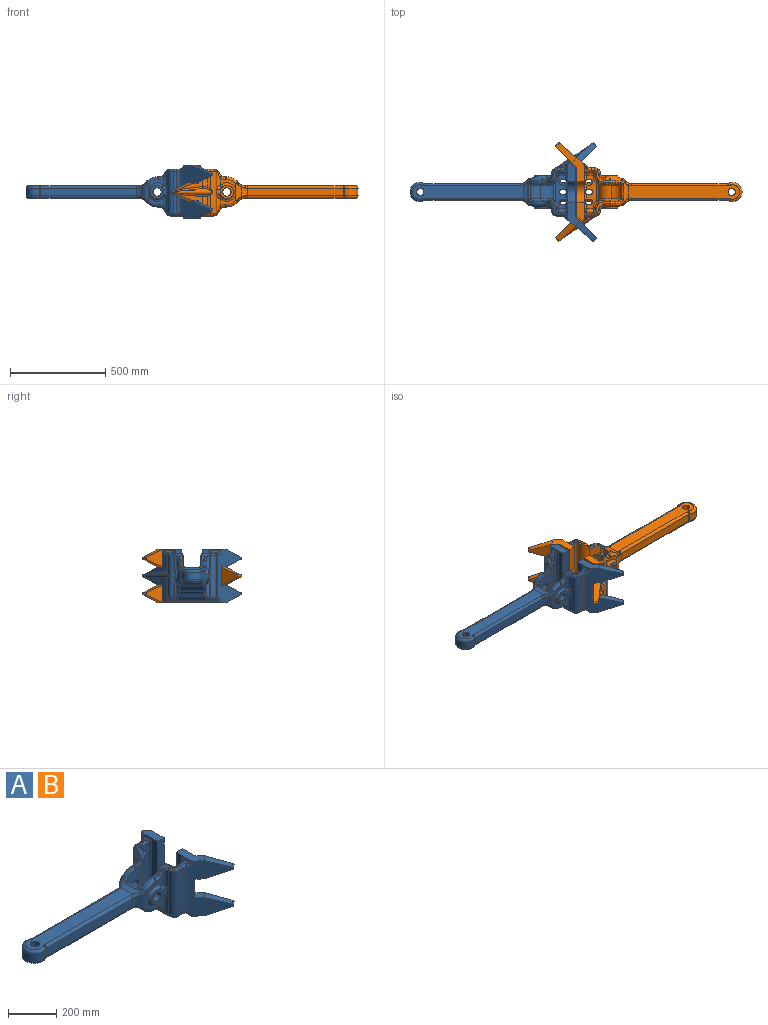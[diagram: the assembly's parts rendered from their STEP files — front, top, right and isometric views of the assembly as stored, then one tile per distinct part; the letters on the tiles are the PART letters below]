
ASSEMBLY  parts=2 mates=1
PART A: 264 faces, bbox 988.1x522.1x283.2 mm
  f0: cylinder r=35mm len=91.5mm, axis (0,0,1), area 2200.2mm2, adj f1,f12,f91,f92,f258
  f1: plane 97.01x18.02mm, normal (0,1,0), area 1677.7mm2, adj f0,f35,f90,f260
  f2: cylinder r=12.7mm len=281.12mm, axis (0,-1,0), area 4841.1mm2, adj f3,f10,f92,f93,f137,f138,f243,f247
  f3: plane 243.38x53.47mm, normal (0,0,-1), area 9442.7mm2, adj f2,f53,f89,f90,f91,f134,f135,f136
  f4: cylinder r=12.7mm len=177.8mm, axis (0,-1,0), area 3084.9mm2, adj f5,f45,f162,f174,f243,f247,f250
  f5: plane 180.47x53.47mm, normal (0,0,1), area 5775.7mm2, adj f4,f152,f158,f159,f161,f170,f171,f173
  f6: cylinder r=79.26mm len=62.88mm, axis (0,-1,0), area 746.2mm2, adj f25,f47,f107,f108,f230,f231
  f7: plane 114.5x114.5mm, normal (0.71,0.71,0), area 9766.8mm2, adj f10,f23,f209,f210,f211,f212
  f8: plane 280.16x148.86mm, normal (-0.64,-0.77,0), area 27221.7mm2, adj f9,f10,f98,f119,f120,f138,f207,f208
  f9: plane 125.59x65.04mm, normal (0,0,1), area 4853mm2, adj f8,f11,f23,f45,f120,f177,f208
  f10: plane 334.61x65.11mm, normal (0,0,-1), area 12374.9mm2, adj f2,f7,f8,f12,f23,f93,f138,f206
  f11: plane 114.5x114.5mm, normal (0.71,0.71,0), area 9766.8mm2, adj f9,f23,f207,f208,f214,f215
  f12: plane 280.16x148.86mm, normal (-0.64,0.77,0), area 10301.5mm2, adj f0,f10,f40,f41,f73,f74,f93,f200
  f13: plane 114.5x114.5mm, normal (0.71,-0.71,0), area 9766.8mm2, adj f23,f201,f202,f203,f204,f205
  f14: plane 81.6x66.55mm, normal (0,-1,0), area 1880.2mm2, adj f19,f96,f127,f128,f129,f188
  f15: plane 81.6x66.55mm, normal (0,1,0), area 1880.2mm2, adj f17,f38,f62,f63,f64,f195
  f16: plane 96.87x2.23mm, normal (-1,0,0), area 209.3mm2, adj f35,f37,f87,f192
  f17: cylinder r=20mm len=86.51mm, axis (0,0,1), area 2196.7mm2, adj f15,f36,f65,f66,f197
  f18: plane 91.49x2.24mm, normal (-1,0,0), area 197.4mm2, adj f21,f94,f113,f183
  f19: cylinder r=20mm len=91.89mm, axis (0,0,1), area 2292.1mm2, adj f14,f95,f130,f131,f189
  f20: plane 81.6x66.55mm, normal (0,1,0), area 1880.2mm2, adj f37,f38,f82,f83,f84,f191
  f21: cylinder r=20mm len=86.51mm, axis (0,0,1), area 2196.7mm2, adj f18,f22,f111,f112,f182
  f22: plane 81.6x66.55mm, normal (0,-1,0), area 1880.2mm2, adj f21,f96,f108,f109,f110,f184
  f23: plane 279.4x254mm, normal (1,0,0), area 51653.5mm2, adj f7,f9,f10,f11,f13,f40,f175,f176
  f24: plane 9.53x5.51mm, normal (0,0,1), area 52.5mm2, adj f26,f28,f63,f224
  f25: plane 9.53x5.51mm, normal (0,0,1), area 52.5mm2, adj f6,f27,f109,f232
  f26: cylinder r=38.1mm len=33.89mm, axis (0,-1,0), area 441.2mm2, adj f24,f29,f64,f65,f222,f223
  f27: cylinder r=38.1mm len=33.89mm, axis (0,-1,0), area 441.2mm2, adj f25,f30,f110,f111,f233,f234
  f28: cylinder r=79.26mm len=62.88mm, axis (0,-1,0), area 746.2mm2, adj f24,f47,f61,f62,f225,f226
  f29: cylinder r=38.1mm len=58.66mm, axis (0,-1,0), area 932.8mm2, adj f26,f31,f66,f67,f68,f219,f220,f221
  f30: cylinder r=38.1mm len=58.66mm, axis (0,-1,0), area 932.8mm2, adj f27,f44,f112,f113,f114,f235,f236,f237
  f31: plane 53.7x28.24mm, normal (0,0,1), area 441.9mm2, adj f29,f32,f69,f70,f71,f217,f218
  f32: cylinder r=12.7mm len=51.66mm, axis (0,-1,0), area 636.2mm2, adj f31,f45,f72,f73,f216
  f33: cylinder r=12.7mm len=51.66mm, axis (0,-1,0), area 636.2mm2, adj f44,f45,f118,f119,f240
  f34: cylinder r=50.8mm len=101.6mm, axis (0,0,1), area 8478.6mm2, adj f54,f55,f75,f101
  f35: cylinder r=31.75mm len=222.25mm, axis (0,0,1), area 10734.8mm2, adj f1,f16,f36,f42,f68,f69,f88,f89
  f36: plane 91.49x2.24mm, normal (-1,0,0), area 197.4mm2, adj f17,f35,f67,f196
  f37: cylinder r=20mm len=91.89mm, axis (0,0,1), area 2292.1mm2, adj f16,f20,f85,f86,f190
  f38: cylinder r=38.1mm len=93mm, axis (0,0,1), area 2472.3mm2, adj f15,f20,f43,f60,f61,f80,f81,f193
  f39: plane 503.39x41.28mm, normal (0,1,0), area 20777.3mm2, adj f43,f54,f57,f77
  f40: plane 101x38.1mm, normal (0,0,1), area 3409mm2, adj f12,f23,f45,f74,f176,f200
  f41: cylinder r=35mm len=83.63mm, axis (0,0,1), area 1986.2mm2, adj f12,f42,f71,f72,f257
  f42: plane 90.66x18.02mm, normal (0,1,0), area 1556.8mm2, adj f35,f41,f70,f259,f261
  f43: cylinder r=38.1mm len=55.19mm, axis (0,0,1), area 1571.9mm2, adj f38,f39,f58,f59,f78,f79
  f44: plane 53.7x28.24mm, normal (0,0,1), area 441.9mm2, adj f30,f33,f115,f116,f117,f238,f239
  f45: plane 281.12x228.6mm, normal (-1,0,0), area 21987.1mm2, adj f4,f9,f32,f33,f40,f74,f120,f145
  f46: plane 583.16x76.2mm, normal (0,0,1), area 35909.7mm2, adj f47,f55,f56,f57,f58,f102,f103,f104
  f47: cylinder r=38.1mm len=119.58mm, axis (0,-1,0), area 2785.4mm2, adj f6,f28,f46,f59,f60,f105,f106,f227
  f48: cylinder r=38.1mm len=132.35mm, axis (0,-1,0), area 5593.3mm2, adj f49,f53,f84,f85,f129,f130
  f49: plane 120.65x5.51mm, normal (0,0,-1), area 665.3mm2, adj f48,f50,f83,f128
  f50: cylinder r=79.26mm len=120.65mm, axis (0,-1,0), area 8758mm2, adj f49,f51,f81,f82,f126,f127
  f51: cylinder r=38.1mm len=119.58mm, axis (0,-1,0), area 3335.1mm2, adj f50,f52,f79,f80,f124,f125
  f52: plane 583.16x76.2mm, normal (0,0,-1), area 35909.7mm2, adj f51,f75,f76,f77,f78,f121,f122,f123
  f53: cylinder r=38.1mm len=223.5mm, axis (0,-1,0), area 7594.5mm2, adj f3,f48,f86,f87,f88,f131,f132,f133
  f54: cylinder r=12.7mm len=41.28mm, axis (0,0,1), area 236.4mm2, adj f34,f39,f56,f76
  f55: torus R=38.1mm, axis (0,0,-1), area 3725.6mm2, adj f34,f46,f56,f102
  f56: torus R=25.4mm, axis (0,0,-1), area 155.8mm2, adj f46,f54,f55,f57
  f57: cylinder r=12.7mm len=503.39mm, axis (1,0,0), area 10042.1mm2, adj f39,f46,f56,f58
  f58: torus R=50.8mm, axis (0,0,-1), area 237.8mm2, adj f43,f46,f57,f59
  f59: bspline ~29.37x28.28mm, area 428.2mm2, adj f43,f47,f58,f60
  f60: bspline ~26.43x23.64mm, area 375.8mm2, adj f38,f47,f59,f61
  f61: bspline ~23.24x21.94mm, area 188.3mm2, adj f28,f38,f60,f62
  f62: torus R=66.56mm, axis (0,-1,0), area 1187.4mm2, adj f15,f28,f61,f63
  f63: cylinder r=12.7mm len=12.7mm, axis (1,0,0), area 110mm2, adj f15,f24,f62,f64
  f64: torus R=50.8mm, axis (0,-1,0), area 506.7mm2, adj f15,f26,f63,f65
  f65: bspline ~30.18x20.89mm, area 329.8mm2, adj f17,f26,f64,f66
  f66: bspline ~32.15x27.43mm, area 525.3mm2, adj f17,f29,f65,f67
  f67: cylinder r=12.7mm len=12.26mm, axis (0,-1,0), area 36.9mm2, adj f29,f36,f66,f68
  f68: bspline ~29.83x21.49mm, area 432.7mm2, adj f29,f35,f67,f69
  f69: torus R=19.05mm, axis (0,0,-1), area 384.7mm2, adj f31,f35,f68,f70
  f70: cylinder r=12.7mm len=18.02mm, axis (1,0,0), area 359.4mm2, adj f31,f42,f69,f71
  f71: torus R=47.7mm, axis (0,0,-1), area 402.5mm2, adj f31,f41,f70,f72
  f72: bspline ~17.57x13.82mm, area 107.2mm2, adj f32,f41,f71,f73
  f73: bspline ~29.24x26.42mm, area 389.8mm2, adj f12,f32,f72,f74
  f74: cylinder r=12.7mm len=9.73mm, axis (0,0,1), area 70.4mm2, adj f12,f40,f45,f73
  f75: torus R=38.1mm, axis (0,0,-1), area 3725.6mm2, adj f34,f52,f76,f121
  f76: torus R=25.4mm, axis (0,0,-1), area 155.8mm2, adj f52,f54,f75,f77
  f77: cylinder r=12.7mm len=503.39mm, axis (-1,0,0), area 10042.1mm2, adj f39,f52,f76,f78
  f78: torus R=50.8mm, axis (0,0,-1), area 237.8mm2, adj f43,f52,f77,f79
  f79: bspline ~29.37x28.28mm, area 428.2mm2, adj f43,f51,f78,f80
  f80: bspline ~29.16x24.11mm, area 375.8mm2, adj f38,f51,f79,f81
  f81: bspline ~23.24x21.94mm, area 188.3mm2, adj f38,f50,f80,f82
  f82: torus R=66.56mm, axis (0,-1,0), area 1187.4mm2, adj f20,f50,f81,f83
  f83: cylinder r=12.7mm len=12.7mm, axis (-1,0,0), area 110mm2, adj f20,f49,f82,f84
  f84: torus R=50.8mm, axis (0,-1,0), area 506.7mm2, adj f20,f48,f83,f85
  f85: bspline ~33.53x21.8mm, area 382.9mm2, adj f37,f48,f84,f86
  f86: bspline ~30.68x28.07mm, area 468.1mm2, adj f37,f53,f85,f87
  f87: cylinder r=12.7mm len=11.77mm, axis (0,-1,0), area 33.5mm2, adj f16,f53,f86,f88
  f88: bspline ~30.06x24.62mm, area 512.1mm2, adj f35,f53,f87,f89
  f89: torus R=19.05mm, axis (0,0,1), area 283.4mm2, adj f3,f35,f88,f90
  f90: cylinder r=12.7mm len=18.02mm, axis (-1,0,0), area 359.4mm2, adj f1,f3,f89,f91
  f91: torus R=47.7mm, axis (0,0,1), area 402.5mm2, adj f0,f3,f90,f92
  f92: bspline ~19.3x15.05mm, area 107.2mm2, adj f0,f2,f91,f93
  f93: bspline ~26.42x25.93mm, area 389.8mm2, adj f2,f10,f12,f92
  f94: cylinder r=31.75mm len=222.25mm, axis (0,0,1), area 11012.1mm2, adj f18,f95,f99,f114,f115,f133,f134,f185
  f95: plane 96.87x2.23mm, normal (-1,0,0), area 209.3mm2, adj f19,f94,f132,f187
  f96: cylinder r=38.1mm len=93mm, axis (0,0,1), area 2472.3mm2, adj f14,f22,f100,f106,f107,f125,f126,f186
  f97: plane 503.39x41.28mm, normal (0,-1,0), area 20777.3mm2, adj f100,f101,f103,f122
  f98: cylinder r=35mm len=224.45mm, axis (0,0,1), area 5437.9mm2, adj f8,f99,f117,f118,f136,f137
  f99: plane 222.25x18.02mm, normal (0,-1,0), area 4004mm2, adj f94,f98,f116,f135
  f100: cylinder r=38.1mm len=55.19mm, axis (0,0,1), area 1571.9mm2, adj f96,f97,f104,f105,f123,f124
  f101: cylinder r=12.7mm len=41.28mm, axis (0,0,1), area 236.4mm2, adj f34,f97,f102,f121
  f102: torus R=25.4mm, axis (0,0,-1), area 155.8mm2, adj f46,f55,f101,f103
  f103: cylinder r=12.7mm len=503.39mm, axis (1,0,0), area 10042.1mm2, adj f46,f97,f102,f104
  f104: torus R=50.8mm, axis (0,0,-1), area 237.8mm2, adj f46,f100,f103,f105
  f105: bspline ~29.37x28.28mm, area 428.2mm2, adj f47,f100,f104,f106
  f106: bspline ~29.16x24.11mm, area 375.8mm2, adj f47,f96,f105,f107
  f107: bspline ~21.91x21.39mm, area 188.3mm2, adj f6,f96,f106,f108
  f108: torus R=66.56mm, axis (0,1,0), area 1187.4mm2, adj f6,f22,f107,f109
  f109: cylinder r=12.7mm len=12.7mm, axis (1,0,0), area 110mm2, adj f22,f25,f108,f110
  f110: torus R=50.8mm, axis (0,1,0), area 506.7mm2, adj f22,f27,f109,f111
  f111: bspline ~30.18x20.89mm, area 329.8mm2, adj f21,f27,f110,f112
  f112: bspline ~32.15x27.43mm, area 525.3mm2, adj f21,f30,f111,f113
  f113: cylinder r=12.7mm len=12.26mm, axis (0,1,0), area 36.9mm2, adj f18,f30,f112,f114
  f114: bspline ~29.83x21.49mm, area 432.7mm2, adj f30,f94,f113,f115
  f115: torus R=19.05mm, axis (0,0,-1), area 384.7mm2, adj f44,f94,f114,f116
  f116: cylinder r=12.7mm len=18.02mm, axis (1,0,0), area 359.4mm2, adj f44,f99,f115,f117
  f117: torus R=47.7mm, axis (0,0,-1), area 402.5mm2, adj f44,f98,f116,f118
  f118: bspline ~18.17x13.82mm, area 107.2mm2, adj f33,f98,f117,f119
  f119: bspline ~29.24x26.42mm, area 389.8mm2, adj f8,f33,f118,f120
  f120: cylinder r=12.7mm len=9.73mm, axis (0,0,1), area 70.4mm2, adj f8,f9,f45,f119
  f121: torus R=25.4mm, axis (0,0,-1), area 155.8mm2, adj f52,f75,f101,f122
  f122: cylinder r=12.7mm len=503.39mm, axis (-1,0,0), area 10042.1mm2, adj f52,f97,f121,f123
  f123: torus R=50.8mm, axis (0,0,-1), area 237.8mm2, adj f52,f100,f122,f124
  f124: bspline ~29.37x28.28mm, area 428.2mm2, adj f51,f100,f123,f125
  f125: bspline ~26.43x23.64mm, area 375.8mm2, adj f51,f96,f124,f126
  f126: bspline ~25.44x24.69mm, area 188.3mm2, adj f50,f96,f125,f127
  f127: torus R=66.56mm, axis (0,1,0), area 1187.4mm2, adj f14,f50,f126,f128
  f128: cylinder r=12.7mm len=12.7mm, axis (-1,0,0), area 110mm2, adj f14,f49,f127,f129
  f129: torus R=50.8mm, axis (0,1,0), area 506.7mm2, adj f14,f48,f128,f130
  f130: bspline ~33.53x21.8mm, area 382.9mm2, adj f19,f48,f129,f131
  f131: bspline ~30.68x28.07mm, area 468.1mm2, adj f19,f53,f130,f132
  f132: cylinder r=12.7mm len=11.77mm, axis (0,1,0), area 33.5mm2, adj f53,f95,f131,f133
  f133: bspline ~32.65x24.62mm, area 512.1mm2, adj f53,f94,f132,f134
  f134: torus R=19.05mm, axis (0,0,1), area 283.4mm2, adj f3,f94,f133,f135
  f135: cylinder r=12.7mm len=18.02mm, axis (-1,0,0), area 359.4mm2, adj f3,f99,f134,f136
  f136: torus R=47.7mm, axis (0,0,1), area 402.5mm2, adj f3,f98,f135,f137
  f137: bspline ~18.17x13.82mm, area 107.2mm2, adj f2,f98,f136,f138
  f138: bspline ~26.42x25.93mm, area 389.8mm2, adj f2,f8,f10,f137
  f139: cylinder r=12.7mm len=203.2mm, axis (0,0,-1), area 4053.7mm2, adj f140,f143,f160,f218,f219
  f140: plane 203.2x6.35mm, normal (1,0,0), area 1290.3mm2, adj f139,f148,f159,f220
  f141: cylinder r=12.7mm len=203.2mm, axis (0,0,-1), area 4053.7mm2, adj f142,f144,f172,f237,f238
  f142: plane 203.2x6.35mm, normal (1,0,0), area 1290.3mm2, adj f141,f164,f171,f236
  f143: plane 203.2x34.93mm, normal (0,-1,0), area 7096.8mm2, adj f139,f145,f161,f217
  f144: plane 203.2x34.93mm, normal (0,1,0), area 7096.8mm2, adj f141,f146,f173,f239
  f145: cylinder r=12.7mm len=222.25mm, axis (0,0,-1), area 4191.8mm2, adj f45,f143,f162,f216
  f146: cylinder r=12.7mm len=222.25mm, axis (0,0,-1), area 4191.8mm2, adj f45,f144,f174,f240
  f147: plane 138.21x85.73mm, normal (0,-1,0), area 7728.2mm2, adj f148,f153,f154,f155,f198,f223,f224,f225
  f148: cylinder r=38.1mm len=203.2mm, axis (0,0,-1), area 11163.9mm2, adj f140,f147,f156,f158,f221,f222
  f149: plane 63.5x38.29mm, normal (1,0,0), area 2431.3mm2, adj f150,f153,f165,f228
  f150: cylinder r=50.8mm len=63.5mm, axis (0,-1,0), area 5364.9mm2, adj f149,f151,f154,f166
  f151: cylinder r=63.5mm len=91.32mm, axis (0,-1,0), area 6007.4mm2, adj f150,f152,f155,f156,f167,f168
  f152: cylinder r=12.7mm len=91.32mm, axis (0,-1,0), area 1435.5mm2, adj f5,f151,f157,f169
  f153: cylinder r=12.7mm len=57.79mm, axis (0,0,-1), area 921.2mm2, adj f147,f149,f154,f226,f227
  f154: torus R=38.1mm, axis (0,-1,0), area 1532.3mm2, adj f147,f150,f153,f155
  f155: torus R=76.2mm, axis (0,-1,0), area 816.2mm2, adj f147,f151,f154,f156
  f156: bspline ~53.16x37.53mm, area 751.6mm2, adj f148,f151,f155,f157
  f157: sphere r=12.7mm, area 120mm2, adj f152,f156,f158
  f158: torus R=50.8mm, axis (0,0,-1), area 692.6mm2, adj f5,f148,f157,f159
  f159: cylinder r=12.7mm len=12.7mm, axis (0,-1,0), area 126.7mm2, adj f5,f140,f158,f160
  f160: sphere r=12.7mm, area 253.4mm2, adj f139,f159,f161
  f161: cylinder r=12.7mm len=34.93mm, axis (-1,0,0), area 696.7mm2, adj f5,f143,f160,f162
  f162: sphere r=12.7mm, area 253.4mm2, adj f4,f145,f161
  f163: plane 138.21x85.73mm, normal (0,1,0), area 7728.2mm2, adj f164,f165,f166,f167,f199,f231,f232,f233
  f164: cylinder r=38.1mm len=203.2mm, axis (0,0,-1), area 11163.9mm2, adj f142,f163,f168,f170,f234,f235
  f165: cylinder r=12.7mm len=57.79mm, axis (0,0,-1), area 921.2mm2, adj f149,f163,f166,f229,f230
  f166: torus R=38.1mm, axis (0,1,0), area 1532.3mm2, adj f150,f163,f165,f167
  f167: torus R=76.2mm, axis (0,1,0), area 816.2mm2, adj f151,f163,f166,f168
  f168: bspline ~53.16x37.53mm, area 751.6mm2, adj f151,f164,f167,f169
  f169: sphere r=12.7mm, area 120mm2, adj f152,f168,f170
  f170: torus R=50.8mm, axis (0,0,-1), area 692.6mm2, adj f5,f164,f169,f171
  f171: cylinder r=12.7mm len=12.7mm, axis (0,1,0), area 126.7mm2, adj f5,f142,f170,f172
  f172: sphere r=12.7mm, area 253.4mm2, adj f141,f171,f173
  f173: cylinder r=12.7mm len=34.93mm, axis (-1,0,0), area 696.7mm2, adj f5,f144,f172,f174
  f174: sphere r=12.7mm, area 253.4mm2, adj f4,f146,f173
  f175: cylinder r=53.98mm len=107.95mm, axis (1,0,0), area 6460.5mm2, adj f23,f45,f176,f177
  f176: plane 136.53x38.1mm, normal (0,-1,0), area 5201.6mm2, adj f23,f40,f45,f175
  f177: plane 136.53x38.1mm, normal (0,1,0), area 5201.6mm2, adj f9,f23,f45,f175
  f178: plane 72.36x72.36mm, normal (0,-1,0), area 2456.3mm2, adj f179,f182,f183,f184,f185,f187,f188,f189
  f179: cylinder r=35.72mm len=12.88mm, axis (0,-1,0), area 0mm2, adj f178,f186
  f180: cylinder r=35.72mm len=12.88mm, axis (0,1,0), area 0mm2, adj f181,f193
  f181: plane 72.36x72.36mm, normal (0,1,0), area 2456.3mm2, adj f180,f190,f191,f192,f194,f195,f196,f197
  f182: bspline ~28.91x20.71mm, area 556.1mm2, adj f21,f178,f183,f184
  f183: bspline ~30.1x22.44mm, area 89.1mm2, adj f18,f178,f182,f185
  f184: torus R=48.42mm, axis (0,1,0), area 1743.8mm2, adj f22,f178,f182,f186
  f185: bspline ~34.19x27.95mm, area 679.7mm2, adj f94,f178,f183,f187
  f186: bspline ~27.73x13.98mm, area 289.5mm2, adj f96,f179,f184,f188
  f187: bspline ~30.65x22.38mm, area 89.1mm2, adj f95,f178,f185,f189
  f188: torus R=48.42mm, axis (0,1,0), area 1743.8mm2, adj f14,f178,f186,f189
  f189: bspline ~28.91x20.71mm, area 556.2mm2, adj f19,f178,f187,f188
  f190: bspline ~28.91x20.71mm, area 556.2mm2, adj f37,f181,f191,f192
  f191: torus R=48.42mm, axis (0,-1,0), area 1743.8mm2, adj f20,f181,f190,f193
  f192: bspline ~30.65x22.38mm, area 89.1mm2, adj f16,f181,f190,f194
  f193: bspline ~27.73x13.98mm, area 289.5mm2, adj f38,f180,f191,f195
  f194: bspline ~34.19x27.95mm, area 679.7mm2, adj f35,f181,f192,f196
  f195: torus R=48.42mm, axis (0,-1,0), area 1743.8mm2, adj f15,f181,f193,f197
  f196: bspline ~29.9x22.37mm, area 89.1mm2, adj f36,f181,f194,f197
  f197: bspline ~28.91x20.71mm, area 556.1mm2, adj f17,f181,f195,f196
  f198: cylinder r=22.23mm len=44.45mm, axis (0,-1,0), area 5763.8mm2, adj f147,f181
  f199: cylinder r=22.23mm len=44.45mm, axis (0,-1,0), area 5763.8mm2, adj f163,f178
  f200: plane 93.66x27.98mm, normal (0.71,0.71,0), area 3705.9mm2, adj f12,f23,f40,f201
  f201: plane 54.92x52.56mm, normal (0,0,1), area 1444mm2, adj f12,f13,f200,f202
  f202: plane 110.11x102.72mm, normal (0.22,0.22,0.95), area 3907.2mm2, adj f12,f13,f201,f203
  f203: cylinder r=6.35mm len=21.29mm, axis (0.71,-0.71,0), area 408.5mm2, adj f12,f13,f202,f204
  f204: plane 110.11x102.72mm, normal (0.22,0.22,-0.95), area 3907.2mm2, adj f12,f13,f203,f205
  f205: plane 54.92x52.56mm, normal (0,0,-1), area 1444mm2, adj f12,f13,f204,f206
  f206: plane 93.66x27.98mm, normal (0.71,0.71,0), area 3705.9mm2, adj f10,f12,f23,f205
  f207: cylinder r=6.35mm len=21.29mm, axis (0.71,0.71,0), area 408.5mm2, adj f8,f11,f208,f215
  f208: plane 110.11x102.72mm, normal (0.22,-0.22,0.95), area 3907.2mm2, adj f8,f9,f11,f207
  f209: plane 110.11x102.72mm, normal (0.22,-0.22,-0.95), area 3907.2mm2, adj f7,f8,f10,f210
  f210: cylinder r=6.35mm len=21.29mm, axis (0.71,0.71,0), area 408.5mm2, adj f7,f8,f209,f211
  f211: plane 110.11x102.72mm, normal (0.22,-0.22,0.95), area 3907.2mm2, adj f7,f8,f210,f212
  f212: plane 54.92x52.56mm, normal (0,0,1), area 1444mm2, adj f7,f8,f211,f213
  f213: plane 95.25x27.98mm, normal (0.71,-0.71,0), area 3768.7mm2, adj f8,f23,f212,f214
  f214: plane 54.92x52.56mm, normal (0,0,-1), area 1444mm2, adj f8,f11,f213,f215
  f215: plane 110.11x102.72mm, normal (0.22,-0.22,-0.95), area 3907.2mm2, adj f8,f11,f207,f214
  f216: bspline ~19.05x19.05mm, area 145.9mm2, adj f32,f145,f217
  f217: cylinder r=6.35mm len=34.93mm, axis (1,0,0), area 348.4mm2, adj f31,f143,f216,f218
  f218: torus R=19.05mm, axis (0,0,-1), area 209.7mm2, adj f31,f139,f217,f219
  f219: bspline ~7.42x6.91mm, area 25.5mm2, adj f29,f139,f218,f220
  f220: cylinder r=6.35mm len=6.4mm, axis (0,-1,0), area 63.7mm2, adj f29,f140,f219,f221
  f221: bspline ~42.87x41.71mm, area 678.4mm2, adj f29,f148,f220,f222
  f222: bspline ~16.68x14.53mm, area 69.9mm2, adj f26,f148,f221,f223
  f223: torus R=44.45mm, axis (0,-1,0), area 376.8mm2, adj f26,f147,f222,f224
  f224: cylinder r=6.35mm len=6.35mm, axis (1,0,0), area 55mm2, adj f24,f147,f223,f225
  f225: torus R=72.91mm, axis (0,-1,0), area 503.2mm2, adj f28,f147,f224,f226
  f226: bspline ~21.98x21.35mm, area 217.8mm2, adj f28,f153,f225,f227
  f227: bspline ~16.72x15.7mm, area 166.7mm2, adj f47,f153,f226,f228
  f228: cylinder r=6.35mm len=63.5mm, axis (0,-1,0), area 927.4mm2, adj f47,f149,f227,f229
  f229: bspline ~16.72x15.7mm, area 166.7mm2, adj f47,f165,f228,f230
  f230: bspline ~21.13x20.67mm, area 217.8mm2, adj f6,f165,f229,f231
  f231: torus R=72.91mm, axis (0,1,0), area 503.2mm2, adj f6,f163,f230,f232
  f232: cylinder r=6.35mm len=6.35mm, axis (-1,0,0), area 55mm2, adj f25,f163,f231,f233
  f233: torus R=44.45mm, axis (0,1,0), area 376.8mm2, adj f27,f163,f232,f234
  f234: bspline ~16.68x14.53mm, area 69.9mm2, adj f27,f164,f233,f235
  f235: bspline ~42.75x40.46mm, area 678.4mm2, adj f30,f164,f234,f236
  f236: cylinder r=6.35mm len=6.4mm, axis (0,-1,0), area 63.7mm2, adj f30,f142,f235,f237
  f237: bspline ~7.42x6.91mm, area 25.5mm2, adj f30,f141,f236,f238
  f238: torus R=19.05mm, axis (0,0,-1), area 209.7mm2, adj f44,f141,f237,f239
  f239: cylinder r=6.35mm len=34.93mm, axis (-1,0,0), area 348.4mm2, adj f44,f144,f238,f240
  f240: bspline ~19.05x19.05mm, area 145.9mm2, adj f33,f146,f239
  f241: plane 25.4x12.7mm, normal (0,1,0), area 322.6mm2, adj f3,f5,f243,f244
  f242: plane 25.4x12.7mm, normal (0,-1,0), area 322.6mm2, adj f3,f5,f243,f244
  f243: cylinder r=12.7mm len=30.97mm, axis (0,0,1), area 1097.2mm2, adj f2,f3,f4,f5,f241,f242
  f244: cylinder r=12.7mm len=25.4mm, axis (0,0,1), area 1013.4mm2, adj f3,f5,f241,f242
  f245: plane 25.4x12.7mm, normal (0,0.89,0.45), area 360.7mm2, adj f3,f5,f247,f248
  f246: plane 25.4x12.7mm, normal (0,-0.89,-0.45), area 360.7mm2, adj f3,f5,f247,f248
  f247: cylinder r=12.7mm len=48.12mm, axis (0,-0.45,0.89), area 1226.8mm2, adj f2,f3,f4,f5,f245,f246
  f248: cylinder r=12.7mm len=48.12mm, axis (0,-0.45,0.89), area 1133mm2, adj f3,f5,f245,f246
  f249: cylinder r=12.7mm len=48.12mm, axis (0,0.45,0.89), area 1133mm2, adj f3,f5,f251,f252
  f250: cylinder r=12.7mm len=48.12mm, axis (0,0.45,0.89), area 1226.8mm2, adj f2,f3,f4,f5,f251,f252
  f251: plane 25.4x12.7mm, normal (0,-0.89,0.45), area 360.7mm2, adj f3,f5,f249,f250
  f252: plane 25.4x12.7mm, normal (0,0.89,-0.45), area 360.7mm2, adj f3,f5,f249,f250
  f253: cylinder r=12.7mm len=199.93mm, axis (-0.83,-0.56,0), area 4870.6mm2, adj f254,f256,f258,f260,f261,f262
  f254: plane 100.53x67.17mm, normal (-0.34,0.51,0.79), area 857.6mm2, adj f253,f255,f257,f259
  f255: cylinder r=12.7mm len=77.7mm, axis (-0.76,-0.64,0.08), area 1131.1mm2, adj f12,f254,f256,f257
  f256: bspline ~163.1x130.84mm, area 2841.9mm2, adj f12,f253,f255,f258
  f257: bspline ~22.5x12.96mm, area 250mm2, adj f41,f254,f255,f259
  f258: bspline ~26.05x17.36mm, area 350.1mm2, adj f0,f253,f256,f260
  f259: cylinder r=12.7mm len=16.66mm, axis (-0.92,0,-0.39), area 177.5mm2, adj f42,f254,f257,f261
  f260: bspline ~20.4x15.26mm, area 240.4mm2, adj f1,f253,f258,f262
  f261: bspline ~11.5x9.95mm, area 69.2mm2, adj f42,f253,f259,f262
  f262: bspline ~38.82x21.02mm, area 269.5mm2, adj f35,f253,f260,f261
  f263: cylinder r=19.45mm len=66.68mm, axis (0,0,1), area 8146.9mm2, adj f46,f52
PART B: same geometry as A
PLACE A at identity
PLACE B rot(axis=(0,0,1),180deg) t=(10,0,0)mm
MATE fastened B.f175 <-> A.f175  axis (-1,0,0) through (10,0,3.17)mm
